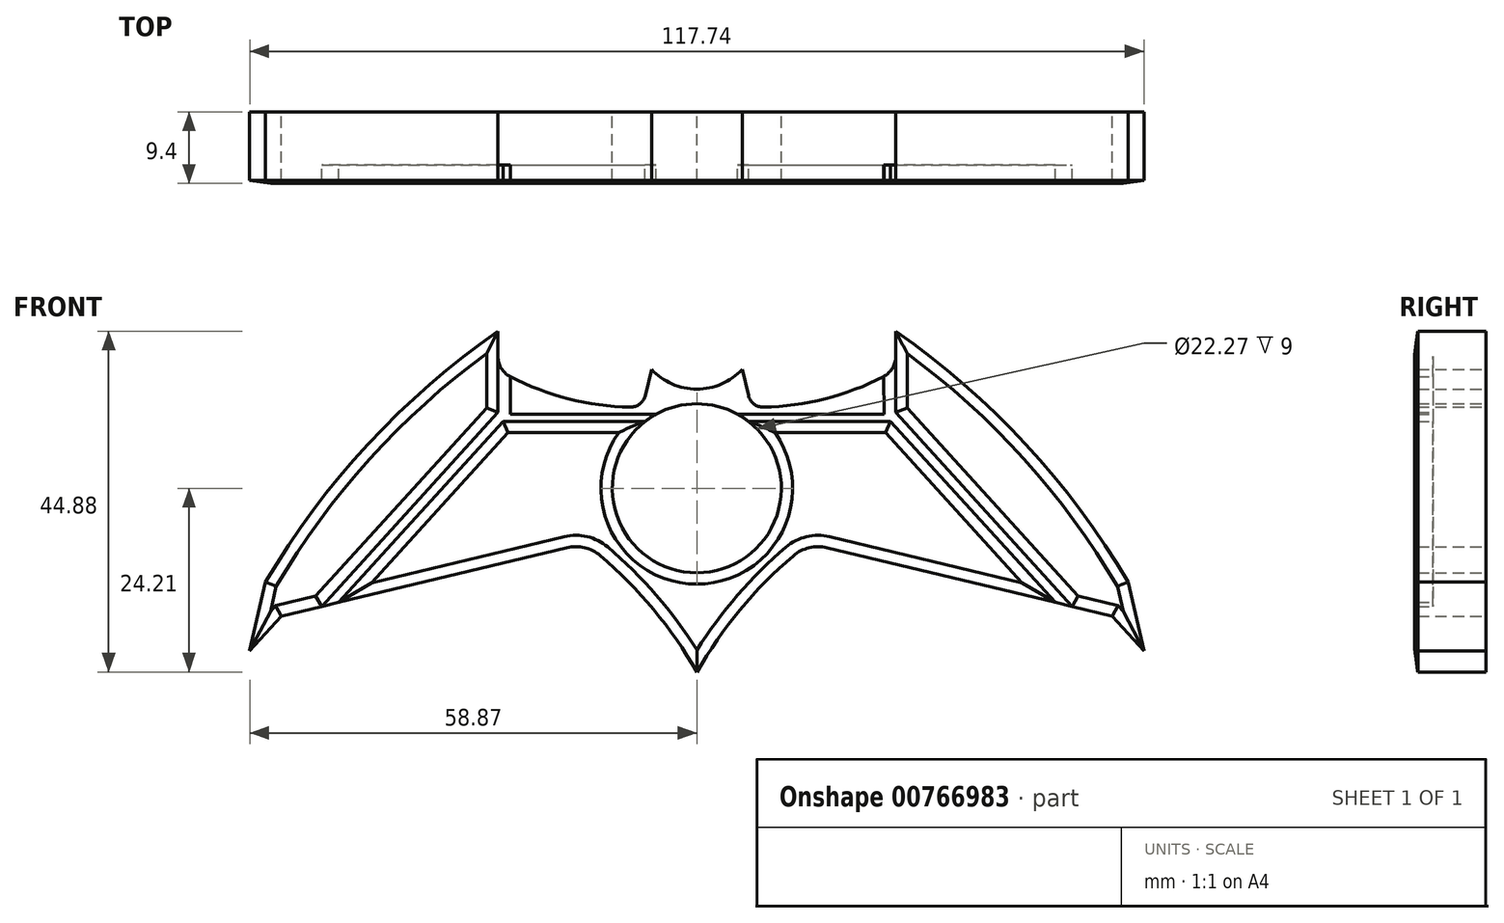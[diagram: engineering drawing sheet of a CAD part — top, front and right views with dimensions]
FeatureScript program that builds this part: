
annotation { "Feature Type Name" : "Feature", "Feature Type Description" : "" }
export const myFeature = defineFeature(function(context is Context, id is Id, definition is map)
    precondition{}
    {
        {
            var Q0;
            Q0=qCreatedBy(makeId("Front.planeOp"),FACE);
            var sketch = newSketch(context, id + "F0", { "sketchPlane" : qUnion([Q0])});
            skLineSegment(sketch, "E0", {"start": v(58.87, -9.1) * mm, "end": v(54.7, -4.48) * mm});
            skLineSegment(sketch, "E1.MirrorCS", {"start": v(-58.87, -9.1) * mm, "end": v(-54.7, -4.48) * mm});
            skArc(sketch, "E2", {"start": v(12.7, 3.46) * mm, "mid": v(5.7, -3.65) * mm, "end": v(0, -11.86) * mm});
            skArc(sketch, "E3", {"start": v(0, -11.86) * mm, "mid": v(-5.68, -3.64) * mm, "end": v(-12.71, 3.48) * mm});
            skLineSegment(sketch, "E4", {"start": v(17.12, 4.52) * mm, "end": v(54.7, -4.48) * mm});
            skLineSegment(sketch, "E5", {"start": v(-54.7, -4.48) * mm, "end": v(-17.11, 4.53) * mm});
            skPoint(sketch, "E6.visualSharp", {"position": v(14.72, 5.1) * mm});
            skArc(sketch, "E6.filletArc", {"start": v(17.12, 4.52) * mm, "mid": v(14.79, 4.52) * mm, "end": v(12.7, 3.46) * mm});
            skPoint(sketch, "E7.visualSharp", {"position": v(-14.72, 5.1) * mm});
            skArc(sketch, "E7.filletArc", {"start": v(-12.71, 3.48) * mm, "mid": v(-14.79, 4.53) * mm, "end": v(-17.11, 4.53) * mm});
            skLineSegment(sketch, "E8", {"start": v(26.2, 33.02) * mm, "end": v(26.2, 27.95) * mm});
            skLineSegment(sketch, "E9.MirrorCS", {"start": v(-26.2, 33.02) * mm, "end": v(-26.2, 29.72) * mm});
            skLineSegment(sketch, "E10", {"start": v(5.97, 28) * mm, "end": v(7.16, 23.03) * mm});
            skPoint(sketch, "E11.endSnap0", {"position": v(6.57, 25.52) * mm});
            skLineSegment(sketch, "E12.MirrorCS", {"start": v(-5.97, 28) * mm, "end": v(-6.8, 24.56) * mm});
            skArc(sketch, "E13", {"start": v(-24.58, 27.06) * mm, "mid": v(-16.91, 24.13) * mm, "end": v(-8.78, 23.03) * mm});
            skArc(sketch, "E14.MirrorCS", {"start": v(26.2, 27.95) * mm, "mid": v(17.02, 24.16) * mm, "end": v(7.16, 23.03) * mm});
            skLineSegment(sketch, "E15", {"start": v(58.87, -9.1) * mm, "end": v(56.78, 0) * mm});
            skPoint(sketch, "E15.endSnap0", {"position": v(56.78, -6.79) * mm});
            skLineSegment(sketch, "E16.MirrorCS", {"start": v(-58.87, -9.1) * mm, "end": v(-56.78, 0) * mm});
            skArc(sketch, "E17", {"start": v(-26.2, 33.02) * mm, "mid": v(-43.29, 18.18) * mm, "end": v(-56.78, 0) * mm});
            skArc(sketch, "E18.MirrorCS", {"start": v(26.2, 33.02) * mm, "mid": v(43.29, 18.18) * mm, "end": v(56.78, 0) * mm});
            skPoint(sketch, "E19.visualSharp", {"position": v(-26.2, 27.95) * mm});
            skArc(sketch, "E19.filletArc", {"start": v(-26.2, 29.72) * mm, "mid": v(-25.76, 28.16) * mm, "end": v(-24.58, 27.06) * mm});
            skPoint(sketch, "E20.MirrorP", {"position": v(26.2, 27.95) * mm});
            skArc(sketch, "E21.MirrorCS", {"start": v(26.2, 29.72) * mm, "mid": v(25.76, 28.16) * mm, "end": v(24.58, 27.06) * mm});
            skArc(sketch, "E22", {"start": v(-5.97, 28) * mm, "mid": v(0, 25.41) * mm, "end": v(5.97, 28) * mm});
            skPoint(sketch, "E23.visualSharp", {"position": v(-7.16, 23.03) * mm});
            skArc(sketch, "E23.filletArc", {"start": v(-8.78, 23.03) * mm, "mid": v(-7.52, 23.45) * mm, "end": v(-6.8, 24.56) * mm});
            skArc(sketch, "E24.MirrorCS", {"start": v(8.78, 23.03) * mm, "mid": v(7.52, 23.45) * mm, "end": v(6.8, 24.56) * mm});
            skCircle(sketch, "E25", {"center": v(0, 12.35) * mm, "radius": 11.13 * mm});
            skSolve(sketch);
        }
        {
            var Q0;
            Q0=qSketchRegion(id+"F0",true);
            extrude(context, id + "F1", {"entities" : qUnion([Q0]), "depth" : 2 * mm});
        }
        {
            var Q0;
            Q0=makeQuery(id+"F1.opExtrude","CAP_FACE",FACE,{"disambiguationData":[OSD([sQuery(id+"F0.wireOp",EDGE,"E0"),sQuery(id+"F0.wireOp",EDGE,"E1.MirrorCS"),sQuery(id+"F0.wireOp",EDGE,"E2"),sQuery(id+"F0.wireOp",EDGE,"E3"),sQuery(id+"F0.wireOp",EDGE,"E4"),sQuery(id+"F0.wireOp",EDGE,"E5"),sQuery(id+"F0.wireOp",EDGE,"E6.filletArc"),sQuery(id+"F0.wireOp",EDGE,"E7.filletArc"),sQuery(id+"F0.wireOp",EDGE,"E8"),sQuery(id+"F0.wireOp",EDGE,"E9.MirrorCS"),sQuery(id+"F0.wireOp",EDGE,"E10"),sQuery(id+"F0.wireOp",EDGE,"E12.MirrorCS"),sQuery(id+"F0.wireOp",EDGE,"E13"),sQuery(id+"F0.wireOp",EDGE,"E15"),sQuery(id+"F0.wireOp",EDGE,"E16.MirrorCS"),sQuery(id+"F0.wireOp",EDGE,"E14.MirrorCS"),sQuery(id+"F0.wireOp",EDGE,"E17"),sQuery(id+"F0.wireOp",EDGE,"E18.MirrorCS"),sQuery(id+"F0.wireOp",EDGE,"E19.filletArc"),sQuery(id+"F0.wireOp",EDGE,"E21.MirrorCS"),sQuery(id+"F0.wireOp",EDGE,"E22"),sQuery(id+"F0.wireOp",EDGE,"E23.filletArc"),sQuery(id+"F0.wireOp",EDGE,"E24.MirrorCS")])],"isStart":false});
            var sketch = newSketch(context, id + "F2", { "sketchPlane" : qUnion([Q0])});
            skLineSegment(sketch, "E26", {"start": v(-24.58, 27.06) * mm, "end": v(-24.58, 22.1) * mm});
            skLineSegment(sketch, "E27", {"start": v(-24.58, 22.1) * mm, "end": v(24.64, 22.1) * mm});
            skLineSegment(sketch, "E28", {"start": v(24.64, 22.1) * mm, "end": v(24.58, 27.06) * mm});
            skLineSegment(sketch, "E29", {"start": v(-26.2, 29.72) * mm, "end": v(-26.2, 22.35) * mm});
            skLineSegment(sketch, "E30", {"start": v(-26.2, 22.35) * mm, "end": v(-49.4, -3.2) * mm});
            skLineSegment(sketch, "E31", {"start": v(-49.4, -3.2) * mm, "end": v(-47.18, -2.68) * mm});
            skLineSegment(sketch, "E32", {"start": v(-47.18, -2.68) * mm, "end": v(-25.5, 21.16) * mm});
            skLineSegment(sketch, "E33", {"start": v(-25.5, 21.16) * mm, "end": v(25.52, 21.16) * mm});
            skLineSegment(sketch, "E34.MirrorCS", {"start": v(47.18, -2.68) * mm, "end": v(25.5, 21.16) * mm});
            skLineSegment(sketch, "E35.MirrorCS", {"start": v(26.2, 22.35) * mm, "end": v(49.4, -3.2) * mm});
            skLineSegment(sketch, "E36.MirrorCS", {"start": v(26.2, 29.72) * mm, "end": v(26.2, 22.35) * mm});
            skSolve(sketch);
        }
        {
            var Q0;
            {var subQ1=sQuery(id+"F2.wireOp",EDGE,"E32");Q0=makeQuery(id+"F2.imprint","IMPRINT",FACE,{"disambiguationData":[TD([[makeQuery(id+"F2.imprint","IMPRINT",EDGE,{"derivedFrom":subQ1}),-1.0]])]});}
            var Q1;
            Q1=makeQuery(id+"F2.imprint","IMPRINT",FACE,{"disambiguationData":[TD([[makeQuery(id+"F2.imprint","IMPRINT",EDGE,{"derivedFrom":sQuery(id+"F2.wireOp",EDGE,"E26")}),1.0]])]});
            var Q2;
            Q2=makeQuery(id+"F2.imprint","IMPRINT",FACE,{"disambiguationData":[TD([[makeQuery(id+"F2.imprint","IMPRINT",EDGE,{"derivedFrom":sQuery(id+"F2.wireOp",EDGE,"E29")}),-1.0]])]});
            var Q3;
            {var subQ1=sQuery(id+"F2.wireOp",EDGE,"E35.MirrorCS");Q3=makeQuery(id+"F2.imprint","IMPRINT",FACE,{"disambiguationData":[TD([[makeQuery(id+"F2.imprint","IMPRINT",EDGE,{"derivedFrom":subQ1}),1.0]])]});}
            extrude(context, id + "F3", {"entities" : qUnion([Q0, Q1, Q2, Q3]), "operationType" : NewBodyOperationType.ADD, "depth" : 7 * mm, "offsetDistance" : 25 * mm});
        }
        {
            var Q0;
            Q0=makeQuery(id+"F3.opExtrude","CAP_FACE",FACE,{"disambiguationData":[OSD([sQuery(id+"F0.wireOp",EDGE,"E2"),sQuery(id+"F0.wireOp",EDGE,"E3"),sQuery(id+"F0.wireOp",EDGE,"E4"),sQuery(id+"F0.wireOp",EDGE,"E5"),sQuery(id+"F0.wireOp",EDGE,"E6.filletArc"),sQuery(id+"F0.wireOp",EDGE,"E7.filletArc"),sQuery(id+"F2.wireOp",EDGE,"E32"),sQuery(id+"F2.wireOp",EDGE,"E33"),sQuery(id+"F2.wireOp",EDGE,"E34.MirrorCS")])],"isStart":false});
            var sketch = newSketch(context, id + "F4", { "sketchPlane" : qUnion([Q0])});
            skSolve(sketch);
        }
        {
            var Q0;
            Q0=qSketchRegion(id+"F4",true);
            var Q1;
            {var subQ2=sQuery(id+"F2.wireOp",EDGE,"E32");Q1=makeQuery(id+"F4.imprint","IMPRINT",FACE,{"disambiguationData":[TD([[makeQuery(id+"F4.imprint","IMPRINT",EDGE,{"derivedFrom":makeQuery(id+"F3.opExtrude","CAP_EDGE",EDGE,{"disambiguationData":[OSD([subQ2])],"isStart":false})}),-1.0]])]});}
            extrude(context, id + "F5", {"entities" : qUnion([Q0, Q1]), "operationType" : NewBodyOperationType.ADD, "depth" : 0.4 * mm, "hasDraft" : true, "draftAngle" : 75 * degree, "draftPullDirection" : true});
        }
        {
            var Q0;
            Q0=makeQuery(id+"F3.opExtrude","CAP_FACE",FACE,{"disambiguationData":[OSD([sQuery(id+"F0.wireOp",EDGE,"E1.MirrorCS"),sQuery(id+"F0.wireOp",EDGE,"E5"),sQuery(id+"F0.wireOp",EDGE,"E9.MirrorCS"),sQuery(id+"F0.wireOp",EDGE,"E16.MirrorCS"),sQuery(id+"F0.wireOp",EDGE,"E17"),sQuery(id+"F2.wireOp",EDGE,"E29"),sQuery(id+"F2.wireOp",EDGE,"E30")])],"isStart":false});
            var sketch = newSketch(context, id + "F6", { "sketchPlane" : qUnion([Q0])});
            skSolve(sketch);
        }
        {
            var Q0;
            {var subQ1=sQuery(id+"F2.wireOp",EDGE,"E30");Q0=makeQuery(id+"F6.imprint","IMPRINT",FACE,{"disambiguationData":[TD([[makeQuery(id+"F6.imprint","IMPRINT",EDGE,{"derivedFrom":makeQuery(id+"F3.opExtrude","CAP_EDGE",EDGE,{"disambiguationData":[OSD([subQ1])],"isStart":false})}),-1.0]])]});}
            extrude(context, id + "F7", {"entities" : qUnion([Q0]), "operationType" : NewBodyOperationType.ADD, "depth" : .4 * mm, "hasDraft" : true, "draftAngle" : 75 * degree, "draftPullDirection" : true});
        }
        {
            var Q0;
            Q0=makeQuery(id+"F3.opExtrude","CAP_FACE",FACE,{"disambiguationData":[OSD([sQuery(id+"F0.wireOp",EDGE,"E0"),sQuery(id+"F0.wireOp",EDGE,"E4"),sQuery(id+"F0.wireOp",EDGE,"E8"),sQuery(id+"F0.wireOp",EDGE,"E15"),sQuery(id+"F0.wireOp",EDGE,"E18.MirrorCS"),sQuery(id+"F2.wireOp",EDGE,"E35.MirrorCS"),sQuery(id+"F2.wireOp",EDGE,"E36.MirrorCS")])],"isStart":false});
            var sketch = newSketch(context, id + "F8", { "sketchPlane" : qUnion([Q0])});
            skSolve(sketch);
        }
        {
            var Q0;
            {var subQ1=sQuery(id+"F2.wireOp",EDGE,"E35.MirrorCS");Q0=makeQuery(id+"F8.imprint","IMPRINT",FACE,{"disambiguationData":[TD([[makeQuery(id+"F8.imprint","IMPRINT",EDGE,{"derivedFrom":makeQuery(id+"F3.opExtrude","CAP_EDGE",EDGE,{"disambiguationData":[OSD([subQ1])],"isStart":false})}),1.0]])]});}
            extrude(context, id + "F9", {"entities" : qUnion([Q0]), "operationType" : NewBodyOperationType.ADD, "depth" : .4 * mm, "hasDraft" : true, "draftAngle" : 75 * degree, "draftPullDirection" : true});
        }
        {
            var Q0;
            Q0 = qSketchRegion(id + "F0", true);
            extrude(context, id + "F10", {"entities" : qUnion([Q0]), "operationType" : NewBodyOperationType.ADD, "depth" : 7 * mm, "offsetDistance" : 25 * mm});
        }
    });
